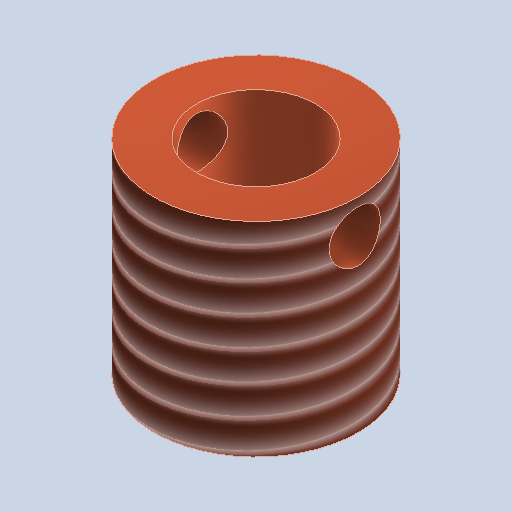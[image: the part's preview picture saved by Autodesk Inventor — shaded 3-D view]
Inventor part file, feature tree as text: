
AUTODESK INVENTOR PART (.ipt)
format: ipt  version: 2025.1 (Build 291241000, 241)  size: 309,760 bytes
history: native  units: mm
features: sketch x3, hole x2, extrude x1, thread x1, plane x1
ambient origin geometry x8: Origin, YZ Plane, XZ Plane, XY Plane, X Axis, Y Axis, Z Axis, Center Point
bodies: Solid1 (feature_tree)
feature tree (8):
  extrude  "Extrusion1"  Depth=12.0mm TaperAngle=0.0deg
  thread  "Thread1"  [1 undecoded]
  plane  "Work Plane1"
  hole  "Hole2"  [1 undecoded]
  hole  "Hole1"  [1 undecoded]
  sketch  "Sketch1"  dims[d0=12.0mm d1=12.0mm d2=0.0mm d3=12.0mm d4=0.0mm]
  sketch  "Sketch2"  dims[d5=7.0mm d6=16.0mm d7=4.0mm d8=2.0mm d9=90.0deg d10=8.0mm d11=0.0mm d12=6.0mm]
  sketch  "Sketch3"  dims[d13=2.0mm d14=3.0mm d15=6.0mm d16=4.0mm d17=2.0mm d18=90.0deg d19=8.0mm d20=0.0mm]
note: 3 required parameter values undecoded (feature->parameter linkage not recoverable at this tier; creation-order binding heuristic only, values carry confidence <= 0.55)
